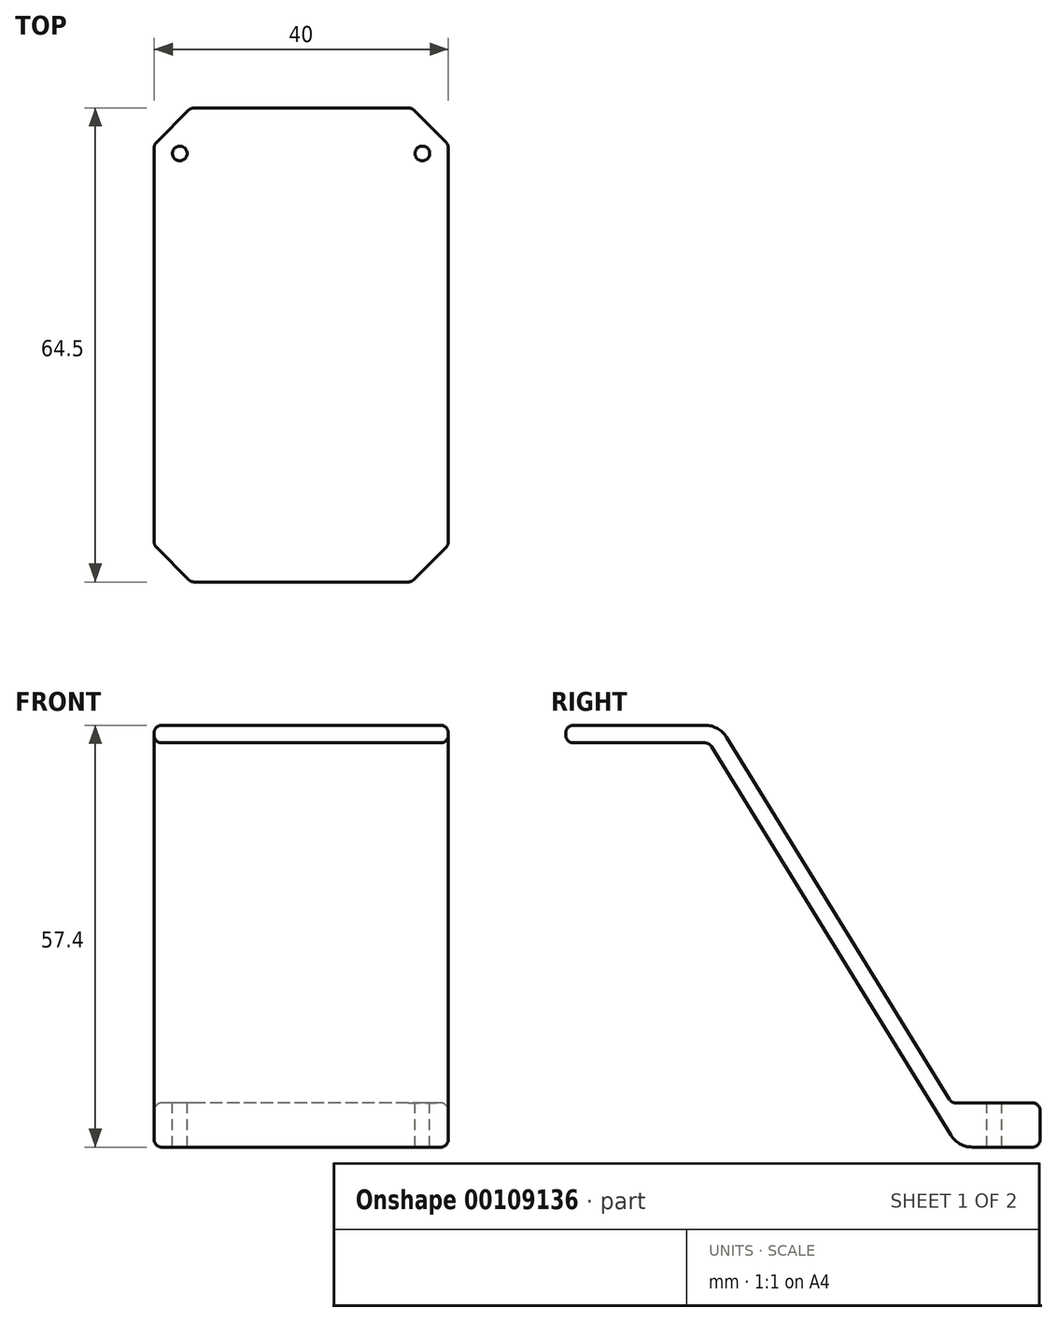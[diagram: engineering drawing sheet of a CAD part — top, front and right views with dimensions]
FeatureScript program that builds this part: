
annotation { "Feature Type Name" : "Feature", "Feature Type Description" : "" }
export const myFeature = defineFeature(function(context is Context, id is Id, definition is map)
    precondition{}
    {
        {
            var Q0;
            Q0=qCreatedBy(makeId("Right.planeOp"),FACE);
            var sketch = newSketch(context, id + "F0", { "sketchPlane" : qUnion([Q0])});
            skLineSegment(sketch, "E0", {"start": v(0, 0) * mm, "end": v(12, 0) * mm});
            skLineSegment(sketch, "E1", {"start": v(12, 0) * mm, "end": v(12, -6) * mm});
            skLineSegment(sketch, "E2", {"start": v(12, -6) * mm, "end": v(0.88, -6) * mm});
            skLineSegment(sketch, "E3", {"start": v(0.88, -6) * mm, "end": v(-33, 49) * mm});
            skLineSegment(sketch, "E4", {"start": v(-33, 49) * mm, "end": v(-52.5, 49) * mm});
            skLineSegment(sketch, "E5", {"start": v(-52.5, 49) * mm, "end": v(-52.5, 51.4) * mm});
            skLineSegment(sketch, "E6", {"start": v(-52.5, 51.4) * mm, "end": v(-31.66, 51.4) * mm});
            skLineSegment(sketch, "E7", {"start": v(-31.66, 51.4) * mm, "end": v(0, 0) * mm});
            skSolve(sketch);
        }
        {
            var Q0;
            Q0=qSketchRegion(id+"F0",true);
            extrude(context, id + "F1", {"entities" : qUnion([Q0]), "depth" : 40 * mm});
        }
        {
            var Q0;
            Q0=makeQuery(id+"F1.opExtrude","SWEPT_FACE",FACE,{"disambiguationData":[OSD([sQuery(id+"F0.wireOp",EDGE,"E0")])]});
            var sketch = newSketch(context, id + "F2", { "sketchPlane" : qUnion([Q0])});
            skCircle(sketch, "E8", {"center": v(3.48, 5.8) * mm, "radius": 1 * mm});
            skCircle(sketch, "E9", {"center": v(36.48, 5.8) * mm, "radius": 1 * mm});
            skLineSegment(sketch, "E10", {"start": v(3.48, 5.8) * mm, "end": v(36.48, 5.8) * mm, "construction": true});
            skLineSegment(sketch, "E11", {"start": v(19.98, 5.8) * mm, "end": v(19.98, 12) * mm, "construction": true});
            skSolve(sketch);
        }
        {
            var Q0;
            Q0=qSketchRegion(id+"F2",true);
            extrude(context, id + "F3", {"entities" : qUnion([Q0]), "operationType" : NewBodyOperationType.REMOVE, "oppositeDirection" : true, "depth" : 25 * mm});
        }
        {
            var Q0;
            Q0=makeQuery(id+"F1.opExtrude","SWEPT_EDGE",EDGE,{"disambiguationData":[OSD([sQuery(id+"F0.wireOp",EDGE,"E0"),sQuery(id+"F0.wireOp",EDGE,"E7")])]});
            var Q1;
            Q1=makeQuery(id+"F1.opExtrude","SWEPT_EDGE",EDGE,{"disambiguationData":[OSD([sQuery(id+"F0.wireOp",EDGE,"E3"),sQuery(id+"F0.wireOp",EDGE,"E4")])]});
            fillet(context, id + "F4", {"entities" : qUnion([Q0, Q1]), "radius" : 1 * mm, "tangentPropagation" : true, "allowEdgeOverflow" : false});
        }
        {
            var Q0;
            Q0=makeQuery(id+"F1.opExtrude","SWEPT_EDGE",EDGE,{"disambiguationData":[OSD([sQuery(id+"F0.wireOp",EDGE,"E6"),sQuery(id+"F0.wireOp",EDGE,"E7")])]});
            var Q1;
            Q1=makeQuery(id+"F1.opExtrude","SWEPT_EDGE",EDGE,{"disambiguationData":[OSD([sQuery(id+"F0.wireOp",EDGE,"E2"),sQuery(id+"F0.wireOp",EDGE,"E3")])]});
            fillet(context, id + "F5", {"entities" : qUnion([Q0, Q1]), "radius" : 3.4 * mm, "tangentPropagation" : true, "allowEdgeOverflow" : false});
        }
        {
            var Q0;
            Q0=makeQuery(id+"F1.opExtrude","CAP_EDGE",EDGE,{"disambiguationData":[OSD([sQuery(id+"F0.wireOp",EDGE,"E5")])],"isStart":false});
            var Q1;
            Q1=makeQuery(id+"F1.opExtrude","CAP_EDGE",EDGE,{"disambiguationData":[OSD([sQuery(id+"F0.wireOp",EDGE,"E1")])],"isStart":false});
            var Q2;
            Q2=makeQuery(id+"F1.opExtrude","CAP_EDGE",EDGE,{"disambiguationData":[OSD([sQuery(id+"F0.wireOp",EDGE,"E5")])],"isStart":true});
            var Q3;
            Q3=makeQuery(id+"F1.opExtrude","CAP_EDGE",EDGE,{"disambiguationData":[OSD([sQuery(id+"F0.wireOp",EDGE,"E1")])],"isStart":true});
            chamfer(context, id + "F6", {"entities" : qUnion([Q0, Q1, Q2, Q3]), "width" : 5 * mm, "tangentPropagation" : true});
        }
        {
            var Q0;
            {var subQ0=sQuery(id+"F0.wireOp",EDGE,"E1");Q0=makeQuery(id+"F6.opChamfer","BLEND_EDGE",EDGE,{"blendedFrom":[makeQuery(id+"F1.opExtrude","CAP_EDGE",EDGE,{"disambiguationData":[OSD([subQ0])],"isStart":true}),makeQuery(id+"F1.opExtrude","SWEPT_FACE",FACE,{"disambiguationData":[OSD([subQ0])]})],"blendedInto":[makeQuery(id+"F1.opExtrude","SWEPT_FACE",FACE,{"disambiguationData":[OSD([subQ0])]})]});}
            var Q1;
            {var subQ0=sQuery(id+"F0.wireOp",EDGE,"E1");Q1=makeQuery(id+"F6.opChamfer","BLEND_EDGE",EDGE,{"blendedFrom":[makeQuery(id+"F1.opExtrude","CAP_EDGE",EDGE,{"disambiguationData":[OSD([subQ0])],"isStart":false}),makeQuery(id+"F1.opExtrude","SWEPT_FACE",FACE,{"disambiguationData":[OSD([subQ0])]})],"blendedInto":[makeQuery(id+"F1.opExtrude","SWEPT_FACE",FACE,{"disambiguationData":[OSD([subQ0])]})]});}
            var Q2;
            {var subQ0=sQuery(id+"F0.wireOp",EDGE,"E5");Q2=makeQuery(id+"F6.opChamfer","BLEND_EDGE",EDGE,{"blendedFrom":[makeQuery(id+"F1.opExtrude","CAP_EDGE",EDGE,{"disambiguationData":[OSD([subQ0])],"isStart":false}),makeQuery(id+"F1.opExtrude","SWEPT_FACE",FACE,{"disambiguationData":[OSD([subQ0])]})],"blendedInto":[makeQuery(id+"F1.opExtrude","SWEPT_FACE",FACE,{"disambiguationData":[OSD([subQ0])]})]});}
            var Q3;
            {var subQ0=sQuery(id+"F0.wireOp",EDGE,"E5");Q3=makeQuery(id+"F6.opChamfer","BLEND_EDGE",EDGE,{"blendedFrom":[makeQuery(id+"F1.opExtrude","CAP_EDGE",EDGE,{"disambiguationData":[OSD([subQ0])],"isStart":true}),makeQuery(id+"F1.opExtrude","SWEPT_FACE",FACE,{"disambiguationData":[OSD([subQ0])]})],"blendedInto":[makeQuery(id+"F1.opExtrude","SWEPT_FACE",FACE,{"disambiguationData":[OSD([subQ0])]})]});}
            fillet(context, id + "F7", {"entities" : qUnion([Q0, Q1, Q2, Q3]), "radius" : 1 * mm, "tangentPropagation" : true, "allowEdgeOverflow" : false});
        }
        {
            var Q0;
            {var subQ0=sQuery(id+"F0.wireOp",EDGE,"E5");Q0=makeQuery(id+"F6.opChamfer","BLEND_EDGE",EDGE,{"blendedFrom":[makeQuery(id+"F1.opExtrude","CAP_EDGE",EDGE,{"disambiguationData":[OSD([subQ0])],"isStart":true}),makeQuery(id+"F1.opExtrude","CAP_FACE",FACE,{"disambiguationData":[OSD([sQuery(id+"F0.wireOp",EDGE,"E0"),sQuery(id+"F0.wireOp",EDGE,"E1"),sQuery(id+"F0.wireOp",EDGE,"E2"),sQuery(id+"F0.wireOp",EDGE,"E3"),sQuery(id+"F0.wireOp",EDGE,"E4"),subQ0,sQuery(id+"F0.wireOp",EDGE,"E6"),sQuery(id+"F0.wireOp",EDGE,"E7")])],"isStart":true})],"blendedInto":[makeQuery(id+"F1.opExtrude","CAP_FACE",FACE,{"disambiguationData":[OSD([sQuery(id+"F0.wireOp",EDGE,"E0"),sQuery(id+"F0.wireOp",EDGE,"E1"),sQuery(id+"F0.wireOp",EDGE,"E2"),sQuery(id+"F0.wireOp",EDGE,"E3"),sQuery(id+"F0.wireOp",EDGE,"E4"),subQ0,sQuery(id+"F0.wireOp",EDGE,"E6"),sQuery(id+"F0.wireOp",EDGE,"E7")])],"isStart":true})]});}
            var Q1;
            {var subQ0=sQuery(id+"F0.wireOp",EDGE,"E1");Q1=makeQuery(id+"F6.opChamfer","BLEND_EDGE",EDGE,{"blendedFrom":[makeQuery(id+"F1.opExtrude","CAP_EDGE",EDGE,{"disambiguationData":[OSD([subQ0])],"isStart":true}),makeQuery(id+"F1.opExtrude","CAP_FACE",FACE,{"disambiguationData":[OSD([sQuery(id+"F0.wireOp",EDGE,"E0"),subQ0,sQuery(id+"F0.wireOp",EDGE,"E2"),sQuery(id+"F0.wireOp",EDGE,"E3"),sQuery(id+"F0.wireOp",EDGE,"E4"),sQuery(id+"F0.wireOp",EDGE,"E5"),sQuery(id+"F0.wireOp",EDGE,"E6"),sQuery(id+"F0.wireOp",EDGE,"E7")])],"isStart":true})],"blendedInto":[makeQuery(id+"F1.opExtrude","CAP_FACE",FACE,{"disambiguationData":[OSD([sQuery(id+"F0.wireOp",EDGE,"E0"),subQ0,sQuery(id+"F0.wireOp",EDGE,"E2"),sQuery(id+"F0.wireOp",EDGE,"E3"),sQuery(id+"F0.wireOp",EDGE,"E4"),sQuery(id+"F0.wireOp",EDGE,"E5"),sQuery(id+"F0.wireOp",EDGE,"E6"),sQuery(id+"F0.wireOp",EDGE,"E7")])],"isStart":true})]});}
            var Q2;
            {var subQ0=sQuery(id+"F0.wireOp",EDGE,"E1");Q2=makeQuery(id+"F6.opChamfer","BLEND_EDGE",EDGE,{"blendedFrom":[makeQuery(id+"F1.opExtrude","CAP_EDGE",EDGE,{"disambiguationData":[OSD([subQ0])],"isStart":false}),makeQuery(id+"F1.opExtrude","CAP_FACE",FACE,{"disambiguationData":[OSD([sQuery(id+"F0.wireOp",EDGE,"E0"),subQ0,sQuery(id+"F0.wireOp",EDGE,"E2"),sQuery(id+"F0.wireOp",EDGE,"E3"),sQuery(id+"F0.wireOp",EDGE,"E4"),sQuery(id+"F0.wireOp",EDGE,"E5"),sQuery(id+"F0.wireOp",EDGE,"E6"),sQuery(id+"F0.wireOp",EDGE,"E7")])],"isStart":false})],"blendedInto":[makeQuery(id+"F1.opExtrude","CAP_FACE",FACE,{"disambiguationData":[OSD([sQuery(id+"F0.wireOp",EDGE,"E0"),subQ0,sQuery(id+"F0.wireOp",EDGE,"E2"),sQuery(id+"F0.wireOp",EDGE,"E3"),sQuery(id+"F0.wireOp",EDGE,"E4"),sQuery(id+"F0.wireOp",EDGE,"E5"),sQuery(id+"F0.wireOp",EDGE,"E6"),sQuery(id+"F0.wireOp",EDGE,"E7")])],"isStart":false})]});}
            var Q3;
            {var subQ0=sQuery(id+"F0.wireOp",EDGE,"E5");Q3=makeQuery(id+"F6.opChamfer","BLEND_EDGE",EDGE,{"blendedFrom":[makeQuery(id+"F1.opExtrude","CAP_EDGE",EDGE,{"disambiguationData":[OSD([subQ0])],"isStart":false}),makeQuery(id+"F1.opExtrude","CAP_FACE",FACE,{"disambiguationData":[OSD([sQuery(id+"F0.wireOp",EDGE,"E0"),sQuery(id+"F0.wireOp",EDGE,"E1"),sQuery(id+"F0.wireOp",EDGE,"E2"),sQuery(id+"F0.wireOp",EDGE,"E3"),sQuery(id+"F0.wireOp",EDGE,"E4"),subQ0,sQuery(id+"F0.wireOp",EDGE,"E6"),sQuery(id+"F0.wireOp",EDGE,"E7")])],"isStart":false})],"blendedInto":[makeQuery(id+"F1.opExtrude","CAP_FACE",FACE,{"disambiguationData":[OSD([sQuery(id+"F0.wireOp",EDGE,"E0"),sQuery(id+"F0.wireOp",EDGE,"E1"),sQuery(id+"F0.wireOp",EDGE,"E2"),sQuery(id+"F0.wireOp",EDGE,"E3"),sQuery(id+"F0.wireOp",EDGE,"E4"),subQ0,sQuery(id+"F0.wireOp",EDGE,"E6"),sQuery(id+"F0.wireOp",EDGE,"E7")])],"isStart":false})]});}
            fillet(context, id + "F8", {"entities" : qUnion([Q0, Q1, Q2, Q3]), "radius" : 1 * mm, "tangentPropagation" : true, "allowEdgeOverflow" : false});
        }
        {
            var Q0;
            Q0=makeQuery(id+"F1.opExtrude","CAP_EDGE",EDGE,{"disambiguationData":[OSD([sQuery(id+"F0.wireOp",EDGE,"E4")])],"isStart":false});
            var Q1;
            Q1=makeQuery(id+"F1.opExtrude","CAP_EDGE",EDGE,{"disambiguationData":[OSD([sQuery(id+"F0.wireOp",EDGE,"E6")])],"isStart":false});
            fillet(context, id + "F9", {"entities" : qUnion([Q0, Q1]), "radius" : 1 * mm, "tangentPropagation" : true, "allowEdgeOverflow" : false});
        }
    });
